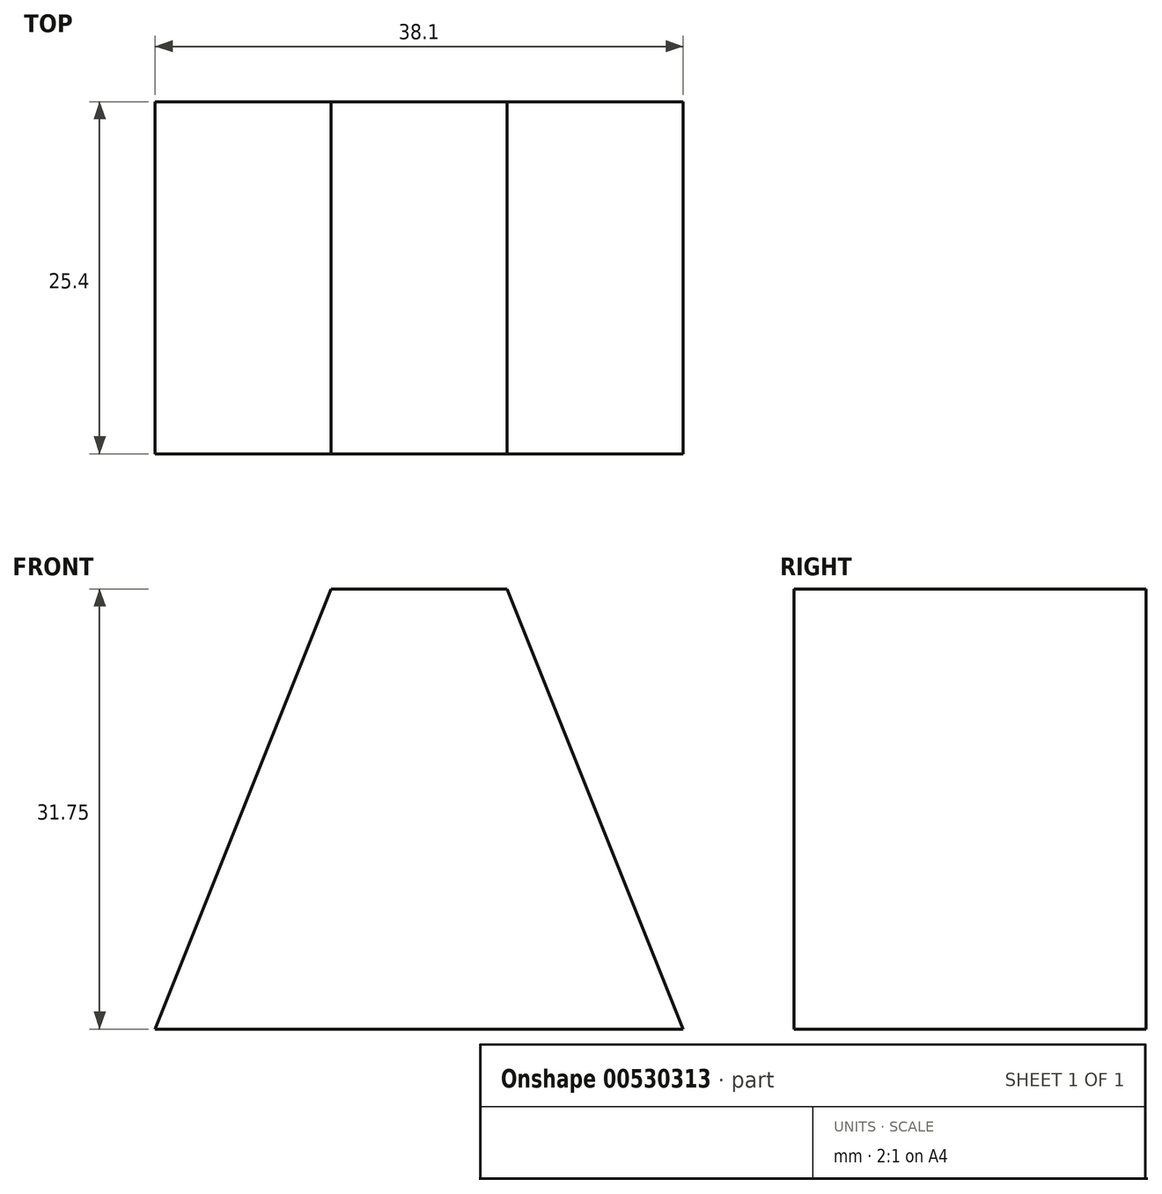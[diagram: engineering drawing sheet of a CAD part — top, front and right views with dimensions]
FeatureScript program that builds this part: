
annotation { "Feature Type Name" : "Feature", "Feature Type Description" : "" }
export const myFeature = defineFeature(function(context is Context, id is Id, definition is map)
    precondition{}
    {
        {
            var Q0;
            Q0=qCreatedBy(makeId("Front.planeOp"),FACE);
            var sketch = newSketch(context, id + "F0", { "sketchPlane" : qUnion([Q0])});
            skLineSegment(sketch, "E0", {"start": v(-54.98, 0) * mm, "end": v(-16.88, 0) * mm});
            skLineSegment(sketch, "E1", {"start": v(-42.28, 0) * mm, "end": v(-42.28, 31.75) * mm});
            skLineSegment(sketch, "E2", {"start": v(-42.28, 31.75) * mm, "end": v(-29.58, 31.75) * mm});
            skLineSegment(sketch, "E3", {"start": v(-29.58, 31.75) * mm, "end": v(-29.58, 0) * mm});
            skLineSegment(sketch, "E4", {"start": v(-29.58, 0) * mm, "end": v(-16.88, 0) * mm});
            skLineSegment(sketch, "E5", {"start": v(-42.28, 0) * mm, "end": v(-54.98, 0) * mm});
            skLineSegment(sketch, "E6", {"start": v(-29.58, 0) * mm, "end": v(-42.28, 0) * mm});
            skLineSegment(sketch, "E7", {"start": v(-42.28, 31.75) * mm, "end": v(-54.98, 0) * mm});
            skLineSegment(sketch, "E8", {"start": v(-29.58, 31.75) * mm, "end": v(-16.88, 0) * mm});
            skLineSegment(sketch, "E9", {"start": v(-42.28, 0) * mm, "end": v(-42.28, 6.35) * mm});
            skLineSegment(sketch, "E10", {"start": v(-42.28, 6.35) * mm, "end": v(-29.58, 6.35) * mm});
            skLineSegment(sketch, "E11", {"start": v(-29.58, 6.35) * mm, "end": v(-29.58, 0) * mm});
            skSolve(sketch);
        }
        {
            var Q0;
            Q0=makeQuery(id+"F0.imprint","IMPRINT",FACE,{"disambiguationData":[TD([[makeQuery(id+"F0.imprint","IMPRINT",EDGE,{"derivedFrom":sQuery(id+"F0.wireOp",EDGE,"E1")}),1.0]])]});
            var Q1;
            Q1=makeQuery(id+"F0.imprint","IMPRINT",FACE,{"disambiguationData":[TD([[makeQuery(id+"F0.imprint","IMPRINT",EDGE,{"derivedFrom":sQuery(id+"F0.wireOp",EDGE,"E1")}),-1.0]])]});
            var Q2;
            Q2=makeQuery(id+"F0.imprint","IMPRINT",FACE,{"disambiguationData":[TD([[makeQuery(id+"F0.imprint","IMPRINT",EDGE,{"derivedFrom":sQuery(id+"F0.wireOp",EDGE,"E3")}),1.0]])]});
            extrude(context, id + "F1", {"entities" : qUnion([Q0, Q1, Q2]), "depth" : 25.4 * mm, "offsetDistance" : 25.4 * mm});
        }
    });
